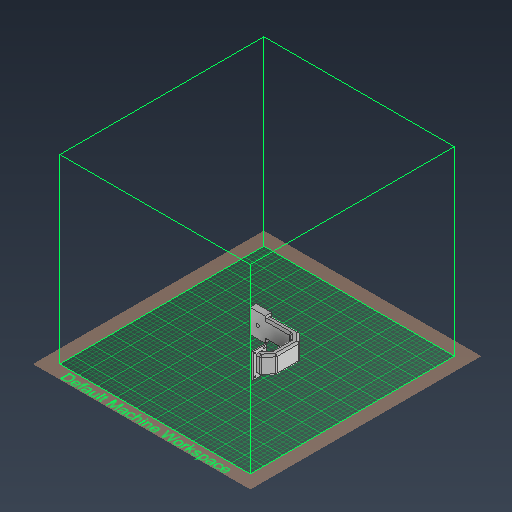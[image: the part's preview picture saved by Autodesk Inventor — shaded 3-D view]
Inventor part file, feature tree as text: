
AUTODESK INVENTOR PART (.ipt)
format: ipt  version: 2021 (Build 250183000, 183)  size: 730,112 bytes
history: native  units: mm
features: sketch x12, fillet x11, extrude x10, sweep x1, shell x1
ambient origin geometry x8: Origin, YZ Plane, XZ Plane, XY Plane, X Axis, Y Axis, Z Axis, Center Point
bodies: Volumenkörper1 (feature_tree)
feature tree (35):
  extrude  "Extrusion1"  Depth=34.2mm
  sweep  "Sweeping1"
  fillet  "Rundung1"  Radius=14.0mm
  fillet  "Rundung2"  Radius=55.9mm
  fillet  "Rundung3"  Radius=90.0mm
  fillet  "Rundung4"  Radius=45.0mm
  fillet  "Rundung5"  Radius=5.0mm
  fillet  "Rundung6"  Radius=58.0mm
  fillet  "Rundung7"  Radius=15.0mm
  fillet  "Rundung8"  [1 undecoded]
  fillet  "Rundung9"  Radius=4.0mm
  shell  "Wandung1"  Thickness=4.0mm
  extrude  "Extrusion2"  Depth=4.0mm
  extrude  "Extrusion3"  Depth=4.0mm
  fillet  "Rundung10"  Radius=4.0mm
  extrude  "Extrusion4"  Depth=4.0mm
  sketch  "Skizze13"  dims[d38=10.0mm d39=0.0mm d40=30.0mm]
  extrude  "Extrusion16"  Depth=2.0mm
  extrude  "Extrusion17"  Depth=10.0mm
  extrude  "Extrusion18"  Depth=2.0mm
  extrude  "Extrusion19"  Depth=2.0mm
  extrude  "Extrusion20"  Depth=5.0mm
  fillet  "Rundung11"  Radius=5.0mm
  extrude  "Extrusion21"  Depth=5.0mm
  sketch  "Skizze1"  dims[d0=52.0mm d1=34.2mm]
  sketch  "Skizze2"  dims[d2=14.0mm d3=0.0mm d4=40.0mm d5=14.0mm d17=55.9mm d18=90.0mm d20=45.0mm d21=5.0mm d22=58.0mm d23=15.0mm d25=0.0mm d26=0.0mm d27=4.0mm d28=4.0mm]
  sketch  "Skizze3"  dims[d29=4.0mm d30=4.0mm]
  sketch  "Skizze4"  dims[d31=4.0mm d32=4.0mm d33=4.0mm]
  sketch  "Skizze5"  dims[d34=4.0mm d35=4.0mm]
  sketch  "Skizze6"  dims[d36=2.0mm d37=2.0mm]
  sketch  "Skizze18"  dims[d41=55.0mm d42=2.0mm]
  sketch  "Skizze20"  dims[d43=3.0mm d44=0.0mm d45=2.0mm]
  sketch  "Skizze21"  dims[d46=3.2mm d47=5.0mm d48=5.0mm]
  sketch  "Skizze22"  dims[d49=3.2mm d50=5.0mm]
  sketch  "Skizze23"  dims[d51=5.0mm d52=3.2mm d53=5.0mm d54=5.0mm d55=3.2mm d56=5.0mm d57=5.0mm d58=3.0mm d59=0.0mm d60=10.0mm d61=36.0mm d62=75.0mm d63=24.668517mm d106=12.0mm d107=25.0mm d108=40.0mm d109=4.5mm d110=0.0mm d111=25.5mm d112=25.5mm d113=12.75mm d114=12.75mm d115=29.0mm d116=29.0mm d117=10.0mm d118=0.0mm d119=3.0mm d120=0.0mm d121=3.2mm d122=3.0mm d123=0.0mm d124=7.0mm d125=8.0mm d126=0.0mm d127=2.0mm d128=2.5mm d129=8.0mm d130=0.0mm]
note: 1 required parameter value undecoded (feature->parameter linkage not recoverable at this tier; creation-order binding heuristic only, values carry confidence <= 0.55)
